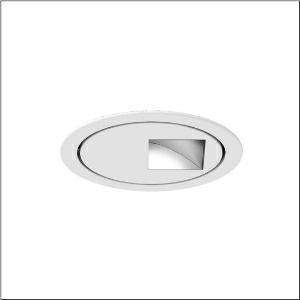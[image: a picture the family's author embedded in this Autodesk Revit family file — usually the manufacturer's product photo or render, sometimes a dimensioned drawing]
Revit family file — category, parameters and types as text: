
# Revit family: lunis_11_mini_round_51dk11b72wn21
name_source: partatom
category: Lighting Fixtures
units: mm (PartAtom-declared; Revit-internal decimal feet)

## family parameters
Cut with Voids When Loaded = No
Host = Face
Light Source = No
Part Type = Normal
Room Calculation Point = No
Round Connector Dimension = Use Diameter
Shared = No

## types (1)
- Lunis 11 mini round (1 x LED 4000K / CRI = 90 (unbekannt), 2120 lm, 4000K)
    Apparent Load = 28 VA
    CIE Flux Codes = 44 77 97 100 100
    Color Rendering = 90
    Color Temperature = 4000K
    Default Elevation = 1800 mm
    Description = Lunis 11 mini round, downlight, light control with wallwasher, of highly reflective aluminium, highly specular, light emission: direct distribution, LED rated luminous flux: 2.120lm, light colour: 940, control gear: ECG, with terminal, 3-pole, mains connection: 220..230V, AC/DC, 0/50..60Hz, LED module, luminaire module, of aluminium, highly specular, white, diameter: 176mm, clamping range: 1..40mm, recessing ring, of plastic, traffic white (RAL 9016), protection rating (complete): IP20, insulation class (complete): insulation class II (safety insulation), certification: CE, permissible ambient temperature for indoor applications: 0..+35°C, packaging unit: 1 piece
    Height = 0 mm  [stored 0 ft]
    Lamp = 1 x LED 4000K / CRI >= 90 (unbekannt)
    Lamp Light Flux = 2120 lm
    Lamp count = 1
    Length = 176 mm
    Luminous efficacy = 75 lm/W
    Manufacturer = Siteco
    ModVariant = No
    Model = 51DK11B72WN21
    Mounting Place = Ceiling
    Mounting Type = Recessed
    Number of Poles = 1
    OnlyDefault = Yes
    Power Factor = 1
    Product Name = Lunis 11 mini round
    Product group = downlight
    ProductGroupID = 400
    Protection Class = Protection class II
    Protection Degree = IP 20
    RLX_Detail_Level = 1
    RLX_Emergency_Light_Flux = 0 lm
    RLX_Emergency_Type = 0
    RLX_Emergency_Type_DB = No
    RlxData = <blob elided: 59333 chars, md5=b60e7bf9>
    Socket = socket
    Standby Power = 0 W
    System Light Flux = 2120 lm
    System Power = 28 W
    Type Comments = Product without accessories
    Type Image = l_1004772.jpg
    URL = http://relux.com
    VarID = ---
    Voltage = 0 V
    Weight = 0.00 kg
    Width = 176 mm

note: [stored X ft] marks values corroborated as IEEE doubles in the binary element streams (Revit-internal decimal feet)

## geometry (parser evidence)
native form markers: Blend x4, Sweep x9
no freeform markers — native parametric forms only
